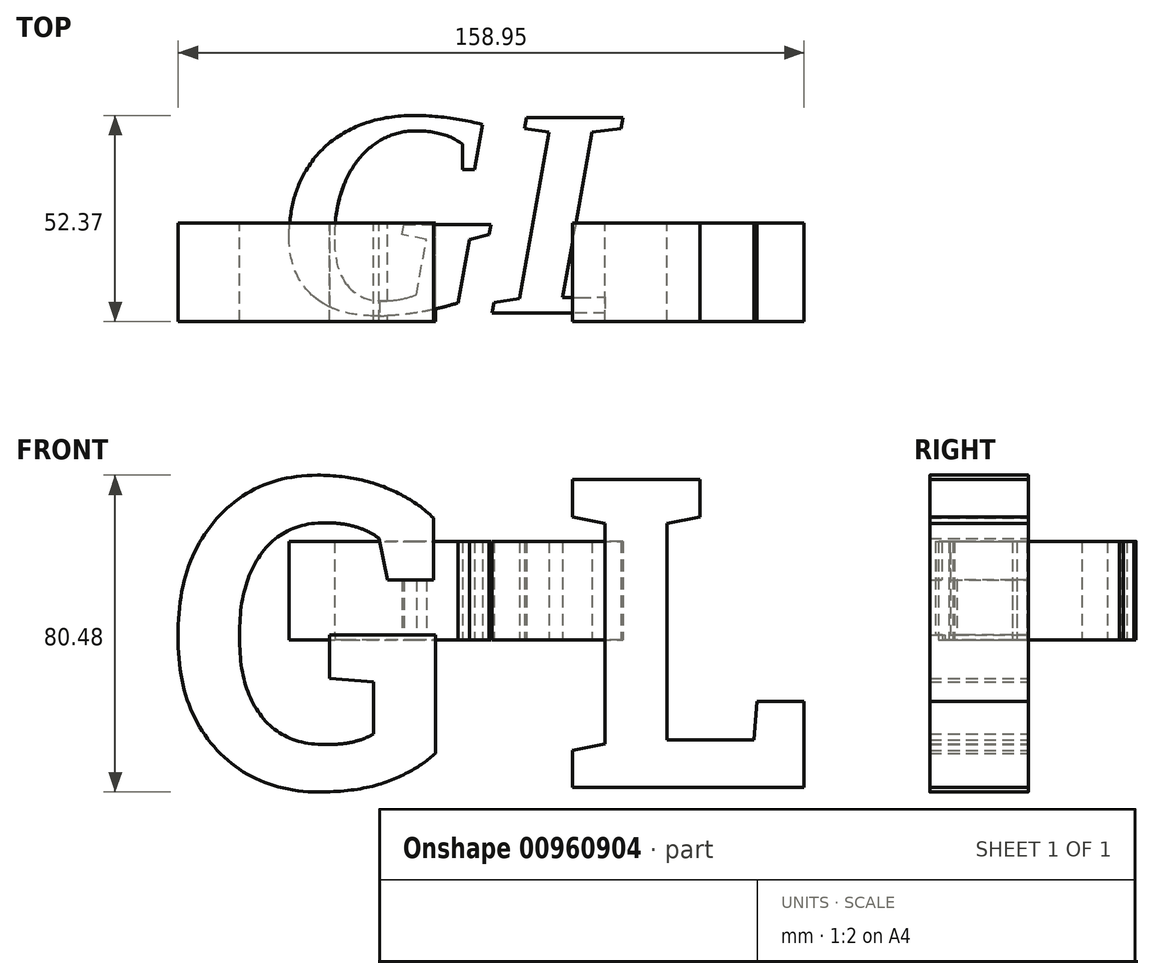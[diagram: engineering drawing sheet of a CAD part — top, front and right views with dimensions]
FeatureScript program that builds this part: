
annotation { "Feature Type Name" : "Feature", "Feature Type Description" : "" }
export const myFeature = defineFeature(function(context is Context, id is Id, definition is map)
    precondition{}
    {
        {
            var Q0;
            Q0=qCreatedBy(makeId("Top.planeOp"),FACE);
            var sketch = newSketch(context, id + "F0", { "sketchPlane" : qUnion([Q0])});
            skText(sketch, "E0", { "text": "GL", "fontName": "Tinos-BoldItalic.ttf"});
            skLineSegment(sketch, "E1", {"start": v(-55.69, 59.2) * mm, "end": v(58.8, 59.2) * mm, "construction": true});
            skLineSegment(sketch, "E2", {"start": v(58.8, 59.2) * mm, "end": v(58.8, -63.24) * mm});
            skLineSegment(sketch, "E3", {"start": v(58.8, -63.24) * mm, "end": v(-65.27, -63.24) * mm});
            skLineSegment(sketch, "E4", {"start": v(-65.27, -63.24) * mm, "end": v(-65.27, 59.2) * mm});
            skLineSegment(sketch, "E5", {"start": v(-65.27, 59.2) * mm, "end": v(-55.69, 59.2) * mm});
            const initialGuessF0  = {"E0": [-0.05569, -0.02279, 1, 0, 0.05454]};
            skSetInitialGuess(sketch, initialGuessF0);
            skSolve(sketch);
        }
        {
            var Q0;
            Q0=makeQuery(id+"F0.imprint","IMPRINT",FACE,{"disambiguationData":[TD([[makeQuery(id+"F0.imprint","IMPRINT",EDGE,{"derivedFrom":sQuery(id+"F0.wireOp",EDGE,"E0.sketch_text.stroke-25")}),-1.0]])]});
            var Q1;
            Q1=makeQuery(id+"F0.imprint","IMPRINT",FACE,{"disambiguationData":[TD([[makeQuery(id+"F0.imprint","IMPRINT",EDGE,{"derivedFrom":sQuery(id+"F0.wireOp",EDGE,"E0.sketch_text.stroke-0")}),-1.0]])]});
            extrude(context, id + "F1", {"entities" : qUnion([Q0, Q1]), "depth" : 25 * mm, "offsetDistance" : 25 * mm});
        }
        {
            var Q0;
            Q0=qCreatedBy(makeId("Front.planeOp"),FACE);
            var sketch = newSketch(context, id + "F2", { "sketchPlane" : qUnion([Q0])});
            skText(sketch, "E6", { "text": "G L", "fontName": "RobotoSlab-Bold.ttf"});
            const initialGuessF2  = {"E6": [-0.0838, -0.03754, 1, 0, 0.07921]};
            skSetInitialGuess(sketch, initialGuessF2);
            skSolve(sketch);
        }
        {
            var Q0;
            Q0=makeQuery(id+"F2.imprint","IMPRINT",FACE,{"disambiguationData":[TD([[makeQuery(id+"F2.imprint","IMPRINT",EDGE,{"derivedFrom":sQuery(id+"F2.wireOp",EDGE,"E6.sketch_text.stroke-0")}),-1.0]])]});
            extrude(context, id + "F3", {"entities" : qUnion([Q0]), "operationType" : NewBodyOperationType.ADD, "depth" : 25 * mm, "offsetDistance" : 25 * mm});
        }
        {
            var Q0;
            Q0=makeQuery(id+"F2.imprint","IMPRINT",FACE,{"disambiguationData":[TD([[makeQuery(id+"F2.imprint","IMPRINT",EDGE,{"derivedFrom":sQuery(id+"F2.wireOp",EDGE,"E6.sketch_text.stroke-26")}),-1.0]])]});
            extrude(context, id + "F4", {"entities" : qUnion([Q0]), "operationType" : NewBodyOperationType.ADD, "depth" : 25 * mm, "offsetDistance" : 25 * mm});
        }
    });
